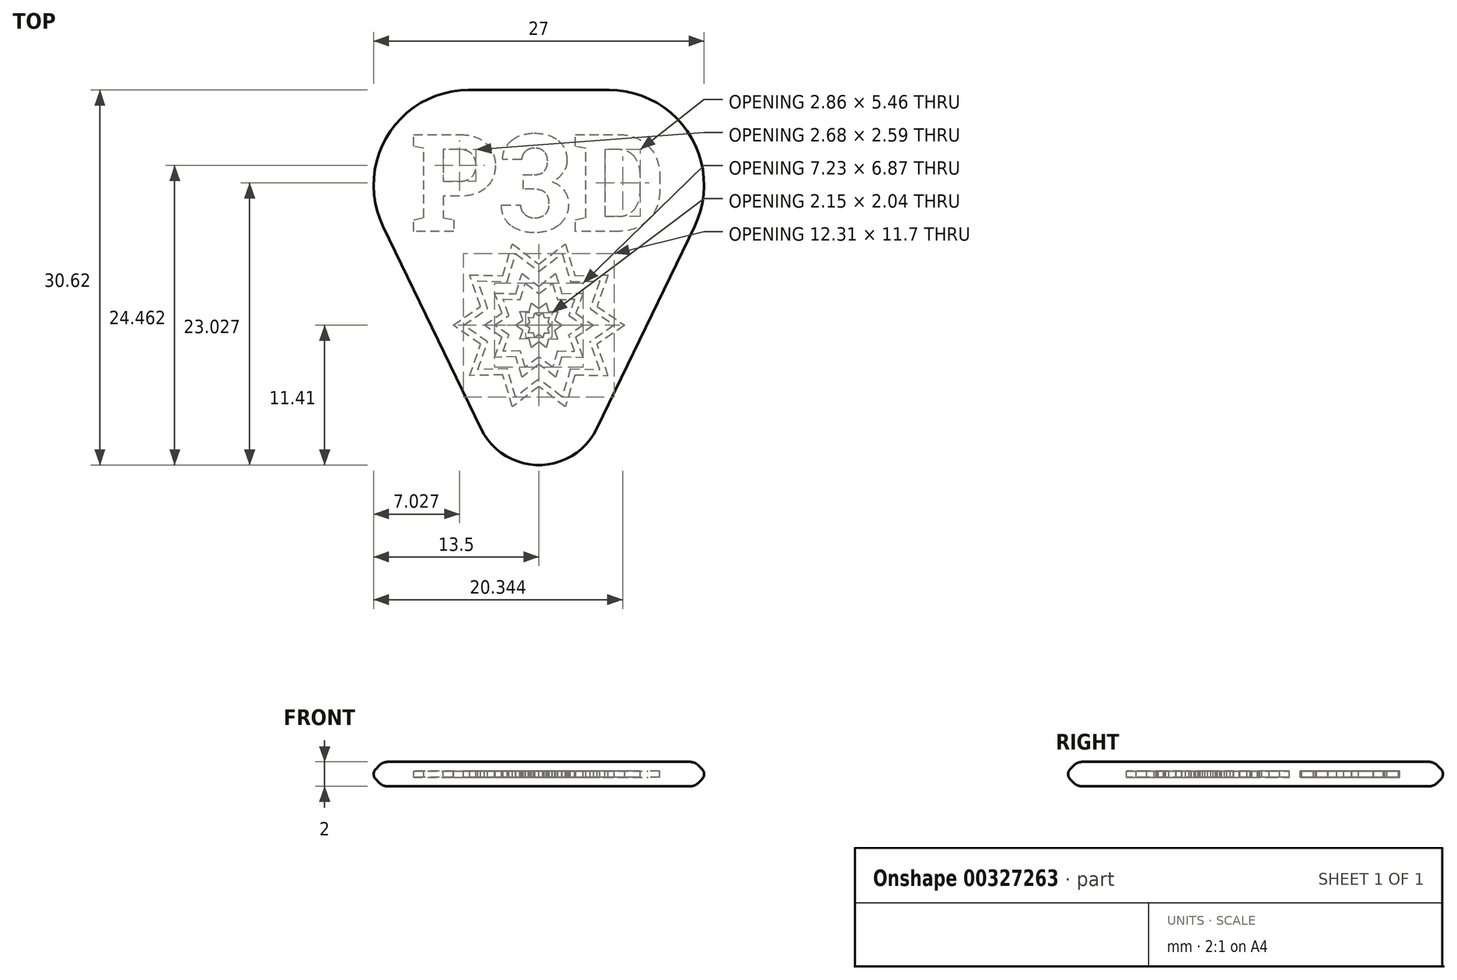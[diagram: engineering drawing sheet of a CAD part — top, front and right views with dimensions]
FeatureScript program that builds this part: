
annotation { "Feature Type Name" : "Feature", "Feature Type Description" : "" }
export const myFeature = defineFeature(function(context is Context, id is Id, definition is map)
    precondition{}
    {
        {
            var Q0;
            Q0=qCreatedBy(makeId("Top.planeOp"),FACE);
            var sketch = newSketch(context, id + "F0", { "sketchPlane" : qUnion([Q0])});
            skLineSegment(sketch, "E0", {"start": v(-5.74, 12.45) * mm, "end": v(5.74, 12.45) * mm});
            skLineSegment(sketch, "E1", {"start": v(12.95, 0.97) * mm, "end": v(4.95, -15.56) * mm});
            skLineSegment(sketch, "E2", {"start": v(-4.95, -15.56) * mm, "end": v(-12.95, 0.97) * mm});
            skPoint(sketch, "E3.visualSharp", {"position": v(-18.5, 12.45) * mm});
            skArc(sketch, "E3.filletArc", {"start": v(-5.74, 12.45) * mm, "mid": v(-12.52, 8.7) * mm, "end": v(-12.95, 0.97) * mm});
            skPoint(sketch, "E4.visualSharp", {"position": v(18.5, 12.45) * mm});
            skArc(sketch, "E4.filletArc", {"start": v(12.95, 0.97) * mm, "mid": v(12.52, 8.7) * mm, "end": v(5.74, 12.45) * mm});
            skPoint(sketch, "E5.visualSharp", {"position": v(0, -25.8) * mm});
            skArc(sketch, "E5.filletArc", {"start": v(-4.95, -15.56) * mm, "mid": v(0, -18.66) * mm, "end": v(4.95, -15.56) * mm});
            skSolve(sketch);
        }
        {
            var Q0;
            Q0=makeQuery(id+"F0.imprint","IMPRINT",FACE,{"disambiguationData":[TD([[makeQuery(id+"F0.imprint","IMPRINT",EDGE,{"derivedFrom":sQuery(id+"F0.wireOp",EDGE,"E0")}),-1.0]])]});
            extrude(context, id + "F1", {"entities" : qUnion([Q0]), "endBound" : BoundingType.SYMMETRIC, "depth" : 2 * mm});
        }
        {
            var Q0;
            Q0=makeQuery(id+"F1.opExtrude","CAP_EDGE",EDGE,{"disambiguationData":[OSD([sQuery(id+"F0.wireOp",EDGE,"E1")])],"isStart":false});
            var Q1;
            Q1=makeQuery(id+"F1.opExtrude","CAP_EDGE",EDGE,{"disambiguationData":[OSD([sQuery(id+"F0.wireOp",EDGE,"E1")])],"isStart":true});
            chamfer(context, id + "F2", {"entities" : qUnion([Q0, Q1]), "chamferType" : ChamferType.OFFSET_ANGLE, "width" : 1 * mm, "oppositeDirection" : false, "angle" : 45 * degree, "tangentPropagation" : true});
        }
        {
            var Q0;
            {var subQ0=sQuery(id+"F0.wireOp",EDGE,"E2");Q0=makeQuery(id+"F2.opChamfer","BLEND_EDGE",EDGE,{"blendedFrom":[makeQuery(id+"F1.opExtrude","CAP_EDGE",EDGE,{"disambiguationData":[OSD([subQ0])],"isStart":false}),makeQuery(id+"F1.opExtrude","CAP_FACE",FACE,{"disambiguationData":[OSD([sQuery(id+"F0.wireOp",EDGE,"E0"),sQuery(id+"F0.wireOp",EDGE,"E1"),subQ0,sQuery(id+"F0.wireOp",EDGE,"E3.filletArc"),sQuery(id+"F0.wireOp",EDGE,"E4.filletArc"),sQuery(id+"F0.wireOp",EDGE,"E5.filletArc")])],"isStart":false})],"blendedInto":[makeQuery(id+"F1.opExtrude","CAP_FACE",FACE,{"disambiguationData":[OSD([sQuery(id+"F0.wireOp",EDGE,"E0"),sQuery(id+"F0.wireOp",EDGE,"E1"),subQ0,sQuery(id+"F0.wireOp",EDGE,"E3.filletArc"),sQuery(id+"F0.wireOp",EDGE,"E4.filletArc"),sQuery(id+"F0.wireOp",EDGE,"E5.filletArc")])],"isStart":false})]});}
            var Q1;
            {var subQ0=sQuery(id+"F0.wireOp",EDGE,"E1");Q1=makeQuery(id+"F2.opChamfer","BLEND_EDGE",EDGE,{"blendedFrom":[makeQuery(id+"F1.opExtrude","CAP_EDGE",EDGE,{"disambiguationData":[OSD([subQ0])],"isStart":true}),makeQuery(id+"F1.opExtrude","CAP_FACE",FACE,{"disambiguationData":[OSD([sQuery(id+"F0.wireOp",EDGE,"E0"),subQ0,sQuery(id+"F0.wireOp",EDGE,"E2"),sQuery(id+"F0.wireOp",EDGE,"E3.filletArc"),sQuery(id+"F0.wireOp",EDGE,"E4.filletArc"),sQuery(id+"F0.wireOp",EDGE,"E5.filletArc")])],"isStart":true})],"blendedInto":[makeQuery(id+"F1.opExtrude","CAP_FACE",FACE,{"disambiguationData":[OSD([sQuery(id+"F0.wireOp",EDGE,"E0"),subQ0,sQuery(id+"F0.wireOp",EDGE,"E2"),sQuery(id+"F0.wireOp",EDGE,"E3.filletArc"),sQuery(id+"F0.wireOp",EDGE,"E4.filletArc"),sQuery(id+"F0.wireOp",EDGE,"E5.filletArc")])],"isStart":true})]});}
            fillet(context, id + "F3", {"entities" : qUnion([Q0, Q1]), "radius" : 1 * mm, "tangentPropagation" : true, "allowEdgeOverflow" : false});
        }
        {
            var Q0;
            Q0=qCreatedBy(makeId("Top.planeOp"),FACE);
            var sketch = newSketch(context, id + "F4", { "sketchPlane" : qUnion([Q0])});
            skText(sketch, "E6", { "text": "P3D", "fontName": "RobotoSlab-Bold.ttf"});
            const initialGuessF4  = {"E6": [-0.01054, 0.00067, 1, 0, 0.008]};
            skSetInitialGuess(sketch, initialGuessF4);
            skSolve(sketch);
        }
        {
            var Q0;
            Q0=qSketchRegion(id+"F4",true);
            extrude(context, id + "F5", {"entities" : qUnion([Q0]), "operationType" : NewBodyOperationType.REMOVE, "endBound" : BoundingType.SYMMETRIC, "oppositeDirection" : true, "depth" : 0.5 * mm});
        }
        {
            var Q0;
            {var subQ0=sQuery(id+"F0.wireOp",EDGE,"E2");Q0=makeQuery(id+"F2.opChamfer","BLEND_EDGE",EDGE,{"blendedFrom":[makeQuery(id+"F1.opExtrude","CAP_EDGE",EDGE,{"disambiguationData":[OSD([subQ0])],"isStart":true}),makeQuery(id+"F1.opExtrude","CAP_EDGE",EDGE,{"disambiguationData":[OSD([subQ0])],"isStart":false})],"blendedInto":[]});}
            fillet(context, id + "F6", {"entities" : qUnion([Q0]), "radius" : 0.6 * mm, "tangentPropagation" : true, "allowEdgeOverflow" : false});
        }
        {
            var Q0;
            Q0=qCreatedBy(makeId("Top.planeOp"),FACE);
            var sketch = newSketch(context, id + "F7", { "sketchPlane" : qUnion([Q0])});
            skCircle(sketch, "E7.cCircle", {"center": v(0, -7) * mm, "radius": 5 * mm, "construction": true});
            skLineSegment(sketch, "E8", {"start": v(-4.76, -5.45) * mm, "end": v(-5.66, -2.89) * mm});
            skLineSegment(sketch, "E9", {"start": v(-5.66, -2.89) * mm, "end": v(-2.94, -2.95) * mm});
            skLineSegment(sketch, "E10", {"start": v(-2.94, -2.95) * mm, "end": v(-2.16, -0.34) * mm});
            skLineSegment(sketch, "E11", {"start": v(-2.16, -0.34) * mm, "end": v(0, -2) * mm});
            skLineSegment(sketch, "E12", {"start": v(0, -2) * mm, "end": v(2.16, -0.34) * mm});
            skLineSegment(sketch, "E13", {"start": v(2.16, -0.34) * mm, "end": v(2.94, -2.95) * mm});
            skLineSegment(sketch, "E14", {"start": v(2.94, -2.95) * mm, "end": v(5.66, -2.89) * mm});
            skLineSegment(sketch, "E15", {"start": v(5.66, -2.89) * mm, "end": v(4.76, -5.45) * mm});
            skLineSegment(sketch, "E16", {"start": v(4.76, -5.45) * mm, "end": v(7, -7) * mm});
            skLineSegment(sketch, "E17", {"start": v(7, -7) * mm, "end": v(4.76, -8.55) * mm});
            skLineSegment(sketch, "E18", {"start": v(2.94, -11.05) * mm, "end": v(5.66, -11.11) * mm});
            skLineSegment(sketch, "E19", {"start": v(5.66, -11.11) * mm, "end": v(4.76, -8.55) * mm});
            skLineSegment(sketch, "E20", {"start": v(2.94, -11.05) * mm, "end": v(2.16, -13.66) * mm});
            skLineSegment(sketch, "E21", {"start": v(2.16, -13.66) * mm, "end": v(0, -12) * mm});
            skLineSegment(sketch, "E22", {"start": v(0, -12) * mm, "end": v(-2.16, -13.66) * mm});
            skLineSegment(sketch, "E23", {"start": v(-2.16, -13.66) * mm, "end": v(-2.94, -11.05) * mm});
            skLineSegment(sketch, "E24", {"start": v(-2.94, -11.05) * mm, "end": v(-5.66, -11.11) * mm});
            skLineSegment(sketch, "E25", {"start": v(-5.66, -11.11) * mm, "end": v(-4.76, -8.55) * mm});
            skLineSegment(sketch, "E26", {"start": v(-4.76, -8.55) * mm, "end": v(-7, -7) * mm});
            skLineSegment(sketch, "E27", {"start": v(-7, -7) * mm, "end": v(-4.76, -5.45) * mm});
            skCircle(sketch, "E28", {"center": v(0, -7) * mm, "radius": 7 * mm, "construction": true});
            skLineSegment(sketch, "E29.0", {"start": v(4.18, -5.64) * mm, "end": v(6.15, -7) * mm});
            skLineSegment(sketch, "E29.1", {"start": v(4.98, -3.38) * mm, "end": v(4.18, -5.64) * mm});
            skLineSegment(sketch, "E29.2", {"start": v(2.58, -3.44) * mm, "end": v(4.98, -3.38) * mm});
            skLineSegment(sketch, "E29.3", {"start": v(1.9, -1.15) * mm, "end": v(2.58, -3.44) * mm});
            skLineSegment(sketch, "E29.4", {"start": v(0, -2.6) * mm, "end": v(1.9, -1.15) * mm});
            skLineSegment(sketch, "E29.5", {"start": v(6.15, -7) * mm, "end": v(4.18, -8.36) * mm});
            skLineSegment(sketch, "E29.6", {"start": v(-1.9, -1.15) * mm, "end": v(0, -2.6) * mm});
            skLineSegment(sketch, "E29.7", {"start": v(-2.58, -3.44) * mm, "end": v(-1.9, -1.15) * mm});
            skLineSegment(sketch, "E29.8", {"start": v(-4.98, -3.38) * mm, "end": v(-2.58, -3.44) * mm});
            skLineSegment(sketch, "E29.9", {"start": v(-4.18, -5.64) * mm, "end": v(-4.98, -3.38) * mm});
            skLineSegment(sketch, "E29.10", {"start": v(1.9, -12.85) * mm, "end": v(0, -11.4) * mm});
            skLineSegment(sketch, "E29.11", {"start": v(2.58, -10.56) * mm, "end": v(1.9, -12.85) * mm});
            skLineSegment(sketch, "E29.12", {"start": v(2.58, -10.56) * mm, "end": v(4.98, -10.62) * mm});
            skLineSegment(sketch, "E29.13", {"start": v(4.98, -10.62) * mm, "end": v(4.18, -8.36) * mm});
            skLineSegment(sketch, "E29.14", {"start": v(0, -11.4) * mm, "end": v(-1.9, -12.85) * mm});
            skLineSegment(sketch, "E29.15", {"start": v(-1.9, -12.85) * mm, "end": v(-2.58, -10.56) * mm});
            skLineSegment(sketch, "E29.16", {"start": v(-2.58, -10.56) * mm, "end": v(-4.98, -10.62) * mm});
            skLineSegment(sketch, "E29.17", {"start": v(-4.98, -10.62) * mm, "end": v(-4.18, -8.36) * mm});
            skLineSegment(sketch, "E29.18", {"start": v(-4.18, -8.36) * mm, "end": v(-6.15, -7) * mm});
            skLineSegment(sketch, "E29.19", {"start": v(-6.15, -7) * mm, "end": v(-4.18, -5.64) * mm});
            skLineSegment(sketch, "E30.0", {"start": v(-4.46, -7) * mm, "end": v(-3.03, -6.02) * mm});
            skLineSegment(sketch, "E30.1", {"start": v(-3.03, -7.98) * mm, "end": v(-4.46, -7) * mm});
            skLineSegment(sketch, "E30.2", {"start": v(-3.6, -9.62) * mm, "end": v(-3.03, -7.98) * mm});
            skLineSegment(sketch, "E30.3", {"start": v(-1.87, -9.58) * mm, "end": v(-3.6, -9.62) * mm});
            skLineSegment(sketch, "E30.4", {"start": v(-1.38, -11.24) * mm, "end": v(-1.87, -9.58) * mm});
            skLineSegment(sketch, "E30.5", {"start": v(-3.03, -6.02) * mm, "end": v(-3.6, -4.38) * mm});
            skLineSegment(sketch, "E30.6", {"start": v(0, -10.19) * mm, "end": v(-1.38, -11.24) * mm});
            skLineSegment(sketch, "E30.7", {"start": v(1.38, -11.24) * mm, "end": v(0, -10.19) * mm});
            skLineSegment(sketch, "E30.8", {"start": v(1.87, -9.58) * mm, "end": v(1.38, -11.24) * mm});
            skLineSegment(sketch, "E30.9", {"start": v(1.87, -9.58) * mm, "end": v(3.6, -9.62) * mm});
            skLineSegment(sketch, "E30.10", {"start": v(0, -3.81) * mm, "end": v(1.38, -2.76) * mm});
            skLineSegment(sketch, "E30.11", {"start": v(-1.38, -2.76) * mm, "end": v(0, -3.81) * mm});
            skLineSegment(sketch, "E30.12", {"start": v(-1.87, -4.42) * mm, "end": v(-1.38, -2.76) * mm});
            skLineSegment(sketch, "E30.13", {"start": v(-3.6, -4.38) * mm, "end": v(-1.87, -4.42) * mm});
            skLineSegment(sketch, "E30.14", {"start": v(1.38, -2.76) * mm, "end": v(1.87, -4.42) * mm});
            skLineSegment(sketch, "E30.15", {"start": v(1.87, -4.42) * mm, "end": v(3.6, -4.38) * mm});
            skLineSegment(sketch, "E30.16", {"start": v(3.6, -4.38) * mm, "end": v(3.03, -6.02) * mm});
            skLineSegment(sketch, "E30.17", {"start": v(3.03, -6.02) * mm, "end": v(4.46, -7) * mm});
            skLineSegment(sketch, "E30.18", {"start": v(4.46, -7) * mm, "end": v(3.03, -7.98) * mm});
            skLineSegment(sketch, "E30.19", {"start": v(3.6, -9.62) * mm, "end": v(3.03, -7.98) * mm});
            skLineSegment(sketch, "E31.0", {"start": v(-2.45, -6.2) * mm, "end": v(-2.92, -4.88) * mm});
            skLineSegment(sketch, "E31.1", {"start": v(-3.61, -7) * mm, "end": v(-2.45, -6.2) * mm});
            skLineSegment(sketch, "E31.2", {"start": v(-2.45, -7.8) * mm, "end": v(-3.61, -7) * mm});
            skLineSegment(sketch, "E31.3", {"start": v(-2.92, -9.12) * mm, "end": v(-2.45, -7.8) * mm});
            skLineSegment(sketch, "E31.4", {"start": v(-1.52, -9.09) * mm, "end": v(-2.92, -9.12) * mm});
            skLineSegment(sketch, "E31.5", {"start": v(-2.92, -4.88) * mm, "end": v(-1.52, -4.91) * mm});
            skLineSegment(sketch, "E31.6", {"start": v(-1.12, -10.44) * mm, "end": v(-1.52, -9.09) * mm});
            skLineSegment(sketch, "E31.7", {"start": v(0, -9.58) * mm, "end": v(-1.12, -10.44) * mm});
            skLineSegment(sketch, "E31.8", {"start": v(1.12, -10.44) * mm, "end": v(0, -9.58) * mm});
            skLineSegment(sketch, "E31.9", {"start": v(1.52, -9.09) * mm, "end": v(1.12, -10.44) * mm});
            skLineSegment(sketch, "E31.10", {"start": v(1.12, -3.56) * mm, "end": v(1.52, -4.91) * mm});
            skLineSegment(sketch, "E31.11", {"start": v(0, -4.42) * mm, "end": v(1.12, -3.56) * mm});
            skLineSegment(sketch, "E31.12", {"start": v(-1.12, -3.56) * mm, "end": v(0, -4.42) * mm});
            skLineSegment(sketch, "E31.13", {"start": v(-1.52, -4.91) * mm, "end": v(-1.12, -3.56) * mm});
            skLineSegment(sketch, "E31.14", {"start": v(1.52, -4.91) * mm, "end": v(2.92, -4.88) * mm});
            skLineSegment(sketch, "E31.15", {"start": v(2.92, -4.88) * mm, "end": v(2.45, -6.2) * mm});
            skLineSegment(sketch, "E31.16", {"start": v(2.45, -6.2) * mm, "end": v(3.61, -7) * mm});
            skLineSegment(sketch, "E31.17", {"start": v(3.61, -7) * mm, "end": v(2.45, -7.8) * mm});
            skLineSegment(sketch, "E31.18", {"start": v(2.92, -9.12) * mm, "end": v(2.45, -7.8) * mm});
            skLineSegment(sketch, "E31.19", {"start": v(1.52, -9.09) * mm, "end": v(2.92, -9.12) * mm});
            skLineSegment(sketch, "E32.0", {"start": v(-1.92, -7) * mm, "end": v(-1.3, -6.58) * mm});
            skLineSegment(sketch, "E32.1", {"start": v(-1.3, -7.42) * mm, "end": v(-1.92, -7) * mm});
            skLineSegment(sketch, "E32.2", {"start": v(-1.55, -8.13) * mm, "end": v(-1.3, -7.42) * mm});
            skLineSegment(sketch, "E32.3", {"start": v(-0.8, -8.1) * mm, "end": v(-1.55, -8.13) * mm});
            skLineSegment(sketch, "E32.4", {"start": v(-0.6, -8.83) * mm, "end": v(-0.8, -8.1) * mm});
            skLineSegment(sketch, "E32.5", {"start": v(-1.3, -6.58) * mm, "end": v(-1.55, -5.87) * mm});
            skLineSegment(sketch, "E32.6", {"start": v(0, -8.37) * mm, "end": v(-0.6, -8.83) * mm});
            skLineSegment(sketch, "E32.7", {"start": v(0.6, -8.83) * mm, "end": v(0, -8.37) * mm});
            skLineSegment(sketch, "E32.8", {"start": v(0.8, -8.1) * mm, "end": v(0.6, -8.83) * mm});
            skLineSegment(sketch, "E32.9", {"start": v(0.8, -8.1) * mm, "end": v(1.55, -8.13) * mm});
            skLineSegment(sketch, "E32.10", {"start": v(0, -5.63) * mm, "end": v(0.6, -5.17) * mm});
            skLineSegment(sketch, "E32.11", {"start": v(-0.6, -5.17) * mm, "end": v(0, -5.63) * mm});
            skLineSegment(sketch, "E32.12", {"start": v(-0.8, -5.9) * mm, "end": v(-0.6, -5.17) * mm});
            skLineSegment(sketch, "E32.13", {"start": v(-1.55, -5.87) * mm, "end": v(-0.8, -5.9) * mm});
            skLineSegment(sketch, "E32.14", {"start": v(0.6, -5.17) * mm, "end": v(0.8, -5.9) * mm});
            skLineSegment(sketch, "E32.15", {"start": v(0.8, -5.9) * mm, "end": v(1.55, -5.87) * mm});
            skLineSegment(sketch, "E32.16", {"start": v(1.55, -5.87) * mm, "end": v(1.3, -6.58) * mm});
            skLineSegment(sketch, "E32.17", {"start": v(1.3, -6.58) * mm, "end": v(1.92, -7) * mm});
            skLineSegment(sketch, "E32.18", {"start": v(1.92, -7) * mm, "end": v(1.3, -7.42) * mm});
            skLineSegment(sketch, "E32.19", {"start": v(1.55, -8.13) * mm, "end": v(1.3, -7.42) * mm});
            skLineSegment(sketch, "E33.0", {"start": v(-0.45, -6.38) * mm, "end": v(-0.33, -5.98) * mm});
            skLineSegment(sketch, "E33.1", {"start": v(-0.87, -6.37) * mm, "end": v(-0.45, -6.38) * mm});
            skLineSegment(sketch, "E33.2", {"start": v(-0.73, -6.76) * mm, "end": v(-0.87, -6.37) * mm});
            skLineSegment(sketch, "E33.3", {"start": v(-1.07, -7) * mm, "end": v(-0.73, -6.76) * mm});
            skLineSegment(sketch, "E33.4", {"start": v(-0.73, -7.24) * mm, "end": v(-1.07, -7) * mm});
            skLineSegment(sketch, "E33.5", {"start": v(-0.33, -5.98) * mm, "end": v(0, -6.23) * mm});
            skLineSegment(sketch, "E33.6", {"start": v(-0.87, -7.63) * mm, "end": v(-0.73, -7.24) * mm});
            skLineSegment(sketch, "E33.7", {"start": v(-0.45, -7.62) * mm, "end": v(-0.87, -7.63) * mm});
            skLineSegment(sketch, "E33.8", {"start": v(-0.33, -8.02) * mm, "end": v(-0.45, -7.62) * mm});
            skLineSegment(sketch, "E33.9", {"start": v(0, -7.77) * mm, "end": v(-0.33, -8.02) * mm});
            skLineSegment(sketch, "E33.10", {"start": v(0.87, -6.37) * mm, "end": v(0.73, -6.76) * mm});
            skLineSegment(sketch, "E33.11", {"start": v(0.45, -6.38) * mm, "end": v(0.87, -6.37) * mm});
            skLineSegment(sketch, "E33.12", {"start": v(0.33, -5.98) * mm, "end": v(0.45, -6.38) * mm});
            skLineSegment(sketch, "E33.13", {"start": v(0, -6.23) * mm, "end": v(0.33, -5.98) * mm});
            skLineSegment(sketch, "E33.14", {"start": v(0.73, -6.76) * mm, "end": v(1.07, -7) * mm});
            skLineSegment(sketch, "E33.15", {"start": v(1.07, -7) * mm, "end": v(0.73, -7.24) * mm});
            skLineSegment(sketch, "E33.16", {"start": v(0.87, -7.63) * mm, "end": v(0.73, -7.24) * mm});
            skLineSegment(sketch, "E33.17", {"start": v(0.45, -7.62) * mm, "end": v(0.87, -7.63) * mm});
            skLineSegment(sketch, "E33.18", {"start": v(0.45, -7.62) * mm, "end": v(0.33, -8.02) * mm});
            skLineSegment(sketch, "E33.19", {"start": v(0.33, -8.02) * mm, "end": v(0, -7.77) * mm});
            skSolve(sketch);
        }
        {
            var Q0;
            Q0 = qSketchRegion(id + "F7", true);
            var Q1;
            Q1=makeQuery(id+"F7.imprint","IMPRINT",FACE,{"disambiguationData":[TD([[makeQuery(id+"F7.imprint","IMPRINT",EDGE,{"derivedFrom":sQuery(id+"F7.wireOp",EDGE,"E30.0")}),-1.0]])]});
            var Q2;
            Q2=makeQuery(id+"F7.imprint","IMPRINT",FACE,{"disambiguationData":[TD([[makeQuery(id+"F7.imprint","IMPRINT",EDGE,{"derivedFrom":sQuery(id+"F7.wireOp",EDGE,"E32.0")}),-1.0]])]});
            extrude(context, id + "F8", {"entities" : qUnion([Q0, Q1, Q2]), "operationType" : NewBodyOperationType.REMOVE, "endBound" : BoundingType.SYMMETRIC, "oppositeDirection" : true, "depth" : 0.5 * mm, "offsetDistance" : 25 * mm});
        }
    });
